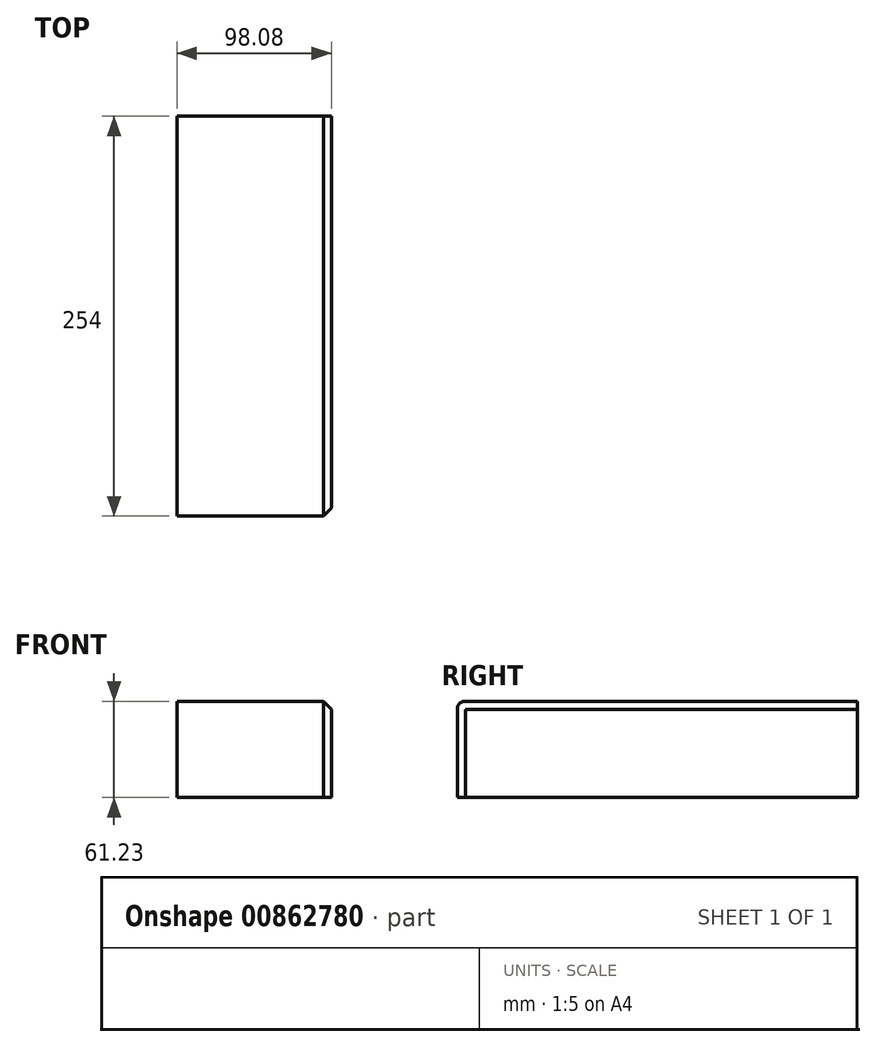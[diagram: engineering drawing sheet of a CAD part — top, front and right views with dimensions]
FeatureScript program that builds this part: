
annotation { "Feature Type Name" : "Feature", "Feature Type Description" : "" }
export const myFeature = defineFeature(function(context is Context, id is Id, definition is map)
    precondition{}
    {
        {
            var Q0;
            Q0=qCreatedBy(makeId("Front.planeOp"),FACE);
            var sketch = newSketch(context, id + "F0", { "sketchPlane" : qUnion([Q0])});
            skLineSegment(sketch, "E0.bottom", {"start": v(0, 0) * mm, "end": v(-98.08, 0) * mm});
            skLineSegment(sketch, "E0.top", {"start": v(0, 61.23) * mm, "end": v(-98.08, 61.23) * mm});
            skLineSegment(sketch, "E0.left", {"start": v(0, 0) * mm, "end": v(0, 61.23) * mm});
            skLineSegment(sketch, "E0.right", {"start": v(-98.08, 0) * mm, "end": v(-98.08, 61.23) * mm});
            skSolve(sketch);
        }
        {
            var Q0;
            Q0=makeQuery(id+"F0.imprint","IMPRINT",FACE,{"disambiguationData":[TD([[makeQuery(id+"F0.imprint","IMPRINT",EDGE,{"derivedFrom":sQuery(id+"F0.wireOp",EDGE,"E0.bottom")}),-1.0]])]});
            extrude(context, id + "F1", {"entities" : qUnion([Q0]), "endBound" : BoundingType.SYMMETRIC, "depth" : 254 * mm, "offsetDistance" : 25.4 * mm});
        }
        {
            var Q0;
            Q0=makeQuery(id+"F1.opExtrude","CAP_EDGE",EDGE,{"disambiguationData":[OSD([sQuery(id+"F0.wireOp",EDGE,"E0.top")])],"isStart":false});
            fillet(context, id + "F2", {"entities" : qUnion([Q0]), "radius" : 5.08 * mm, "tangentPropagation" : true, "allowEdgeOverflow" : false});
        }
        {
            var Q0;
            Q0=makeQuery(id+"F1.opExtrude","SWEPT_EDGE",EDGE,{"disambiguationData":[OSD([sQuery(id+"F0.wireOp",EDGE,"E0.top"),sQuery(id+"F0.wireOp",EDGE,"E0.left")])]});
            chamfer(context, id + "F3", {"entities" : qUnion([Q0]), "width" : 5.08 * mm, "tangentPropagation" : true});
        }
    });
